# Revit family: Ribbeelement - RTP
name_source: partatom
category: Structural Framing
units: mm (PartAtom-declared; Revit-internal decimal feet)

## family parameters
Always export as geometry = No
Always vertical = Yes
Cut with Voids When Loaded = No
Material for Model Behavior = Other
OmniClass Number = 23.25.30.11.14.14
OmniClass Title = Beams
Section Shape = Not Defined
Shared = No
Show family pre-cut in plan views = Yes

## types (8) — shared parameters
Bredde = 2392 mm  [stored 7.84777 ft]
CRH_RFA_TimeStamp_LastRelease = 20191107
Manufacturer = CRH Concrete
Pladebredde 1 = 1196 mm  [stored 3.92388 ft]
Pladebredde 2 = 1196 mm  [stored 3.92388 ft]
Pladetykkelse = 60 mm  [stored 0.19685 ft]
Pladetykkelse Standard = 60 mm  [stored 0.19685 ft]

## per-type parameters (varying)
| type | Højde | Højde Standard | Length Max | Model | Ribbe CC Afstand | Tværsnit RTPA | Tværsnit RTPB |
| RTPA 102 | 1020 mm  [stored 3.34646 ft] | 1020 mm  [stored 3.34646 ft] | 36300 mm  [stored 119.094 ft] | RTPA | 1200 mm  [stored 3.93701 ft] | Yes | No |
| RTPA 72 | 720 mm  [stored 2.3622 ft] | 720 mm  [stored 2.3622 ft] | 24300 mm | RTPA | 1200 mm  [stored 3.93701 ft] | Yes | No |
| RTPA 90 | 900 mm  [stored 2.95276 ft] | 900 mm  [stored 2.95276 ft] | 33400 mm  [stored 109.58 ft] | RTPA | 1200 mm  [stored 3.93701 ft] | Yes | No |
| RTPA 60 | 600 mm  [stored 1.9685 ft] | 600 mm  [stored 1.9685 ft] | 24300 mm | RTPA | 1200 mm  [stored 3.93701 ft] | Yes | No |
| RTPB 102 | 1020 mm  [stored 3.34646 ft] | 1020 mm  [stored 3.34646 ft] | 36000 mm | RTPB | 1800 mm  [stored 5.90551 ft] | No | Yes |
| RTPB 90 | 900 mm  [stored 2.95276 ft] | 900 mm  [stored 2.95276 ft] | 32000 mm  [stored 104.987 ft] | RTPB | 1800 mm  [stored 5.90551 ft] | No | Yes |
| RTPB 72 | 720 mm  [stored 2.3622 ft] | 720 mm  [stored 2.3622 ft] | 24360 mm  [stored 79.9213 ft] | RTPB | 1800 mm  [stored 5.90551 ft] | No | Yes |
| RTPB 60 | 600 mm  [stored 1.9685 ft] | 600 mm  [stored 1.9685 ft] | 24360 mm  [stored 79.9213 ft] | RTPB | 1800 mm  [stored 5.90551 ft] | No | Yes |

note: [stored X ft] marks values corroborated as IEEE doubles in the binary element streams (Revit-internal decimal feet)

## geometry (parser evidence)
native form markers: Sweep x11
no freeform markers — native parametric forms only
